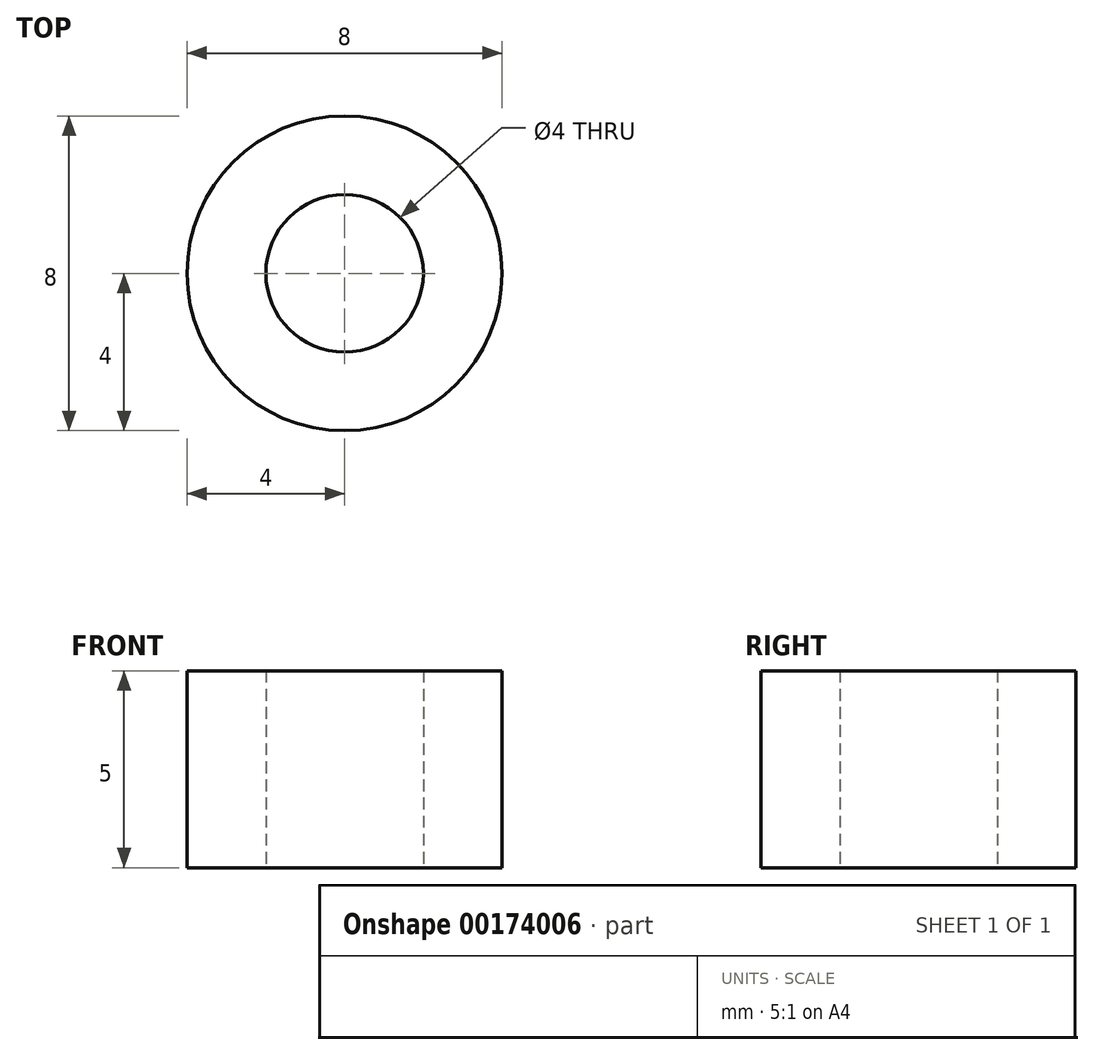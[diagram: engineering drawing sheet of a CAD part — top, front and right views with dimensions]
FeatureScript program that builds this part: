
annotation { "Feature Type Name" : "Feature", "Feature Type Description" : "" }
export const myFeature = defineFeature(function(context is Context, id is Id, definition is map)
    precondition{}
    {
        {
            var Q0;
            Q0=qCreatedBy(makeId("Top.planeOp"),FACE);
            var sketch = newSketch(context, id + "F0", { "sketchPlane" : qUnion([Q0])});
            skCircle(sketch, "E0", {"center": v(0, 0) * mm, "radius": 2 * mm});
            skCircle(sketch, "E1", {"center": v(0, 0) * mm, "radius": 4 * mm});
            skSolve(sketch);
        }
        {
            var Q0;
            Q0 = qSketchRegion(id + "F0", true);
            extrude(context, id + "F1", {"entities" : qUnion([Q0]), "depth" : 5 * mm});
        }
    });
